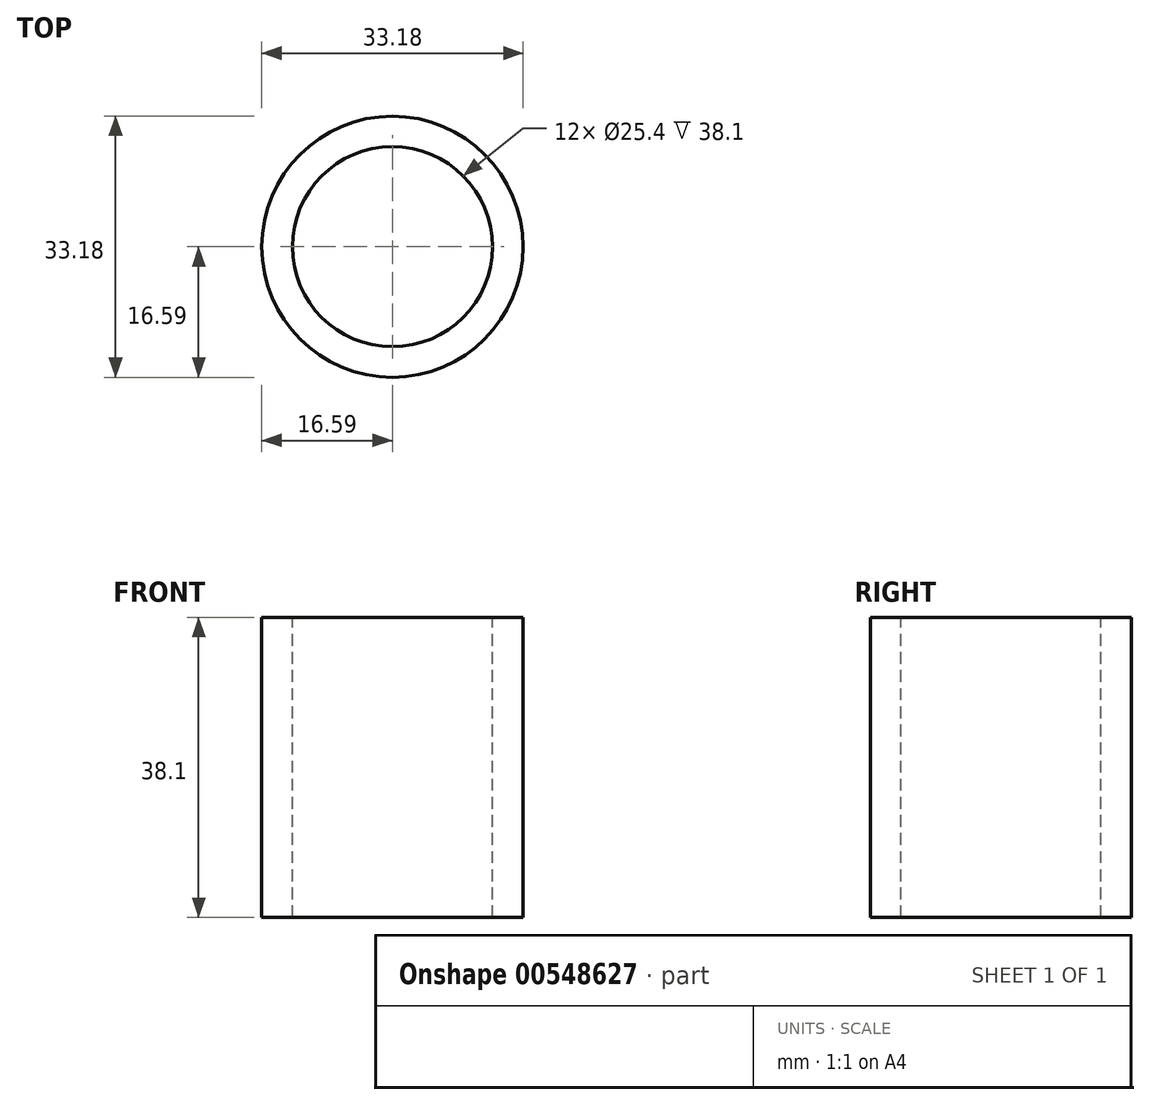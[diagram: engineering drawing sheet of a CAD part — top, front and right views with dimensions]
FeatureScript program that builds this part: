
annotation { "Feature Type Name" : "Feature", "Feature Type Description" : "" }
export const myFeature = defineFeature(function(context is Context, id is Id, definition is map)
    precondition{}
    {
        {
            var Q0;
            Q0=qCreatedBy(makeId("Front.planeOp"),FACE);
            var sketch = newSketch(context, id + "F0", { "sketchPlane" : qUnion([Q0])});
            skLineSegment(sketch, "E0", {"start": v(16.59, 38.1) * mm, "end": v(16.59, 0) * mm});
            skLineSegment(sketch, "E1", {"start": v(16.59, 0) * mm, "end": v(12.7, 0) * mm});
            skLineSegment(sketch, "E2", {"start": v(12.7, 0) * mm, "end": v(12.7, 38.1) * mm});
            skLineSegment(sketch, "E3", {"start": v(12.7, 38.1) * mm, "end": v(16.59, 38.1) * mm});
            skSolve(sketch);
        }
        {
            var Q0;
            Q0=qCreatedBy(makeId("Front.planeOp"),FACE);
            var sketch = newSketch(context, id + "F1", { "sketchPlane" : qUnion([Q0])});
            skLineSegment(sketch, "E4", {"start": v(0, 75.36) * mm, "end": v(0, 0) * mm});
            skSolve(sketch);
        }
        {
            var Q0;
            Q0=makeQuery(id+"F0.imprint","IMPRINT",FACE,{"disambiguationData":[TD([[makeQuery(id+"F0.imprint","IMPRINT",EDGE,{"derivedFrom":sQuery(id+"F0.wireOp",EDGE,"E0")}),-1.0]])]});
            var Q1;
            Q1=sQuery(id+"F1.wireOp",EDGE,"E4");
            revolve(context, id + "F2", {"entities" : qUnion([Q0]), "axis" : qUnion([Q1]), "revolveType" : RevolveType.FULL});
        }
    });
